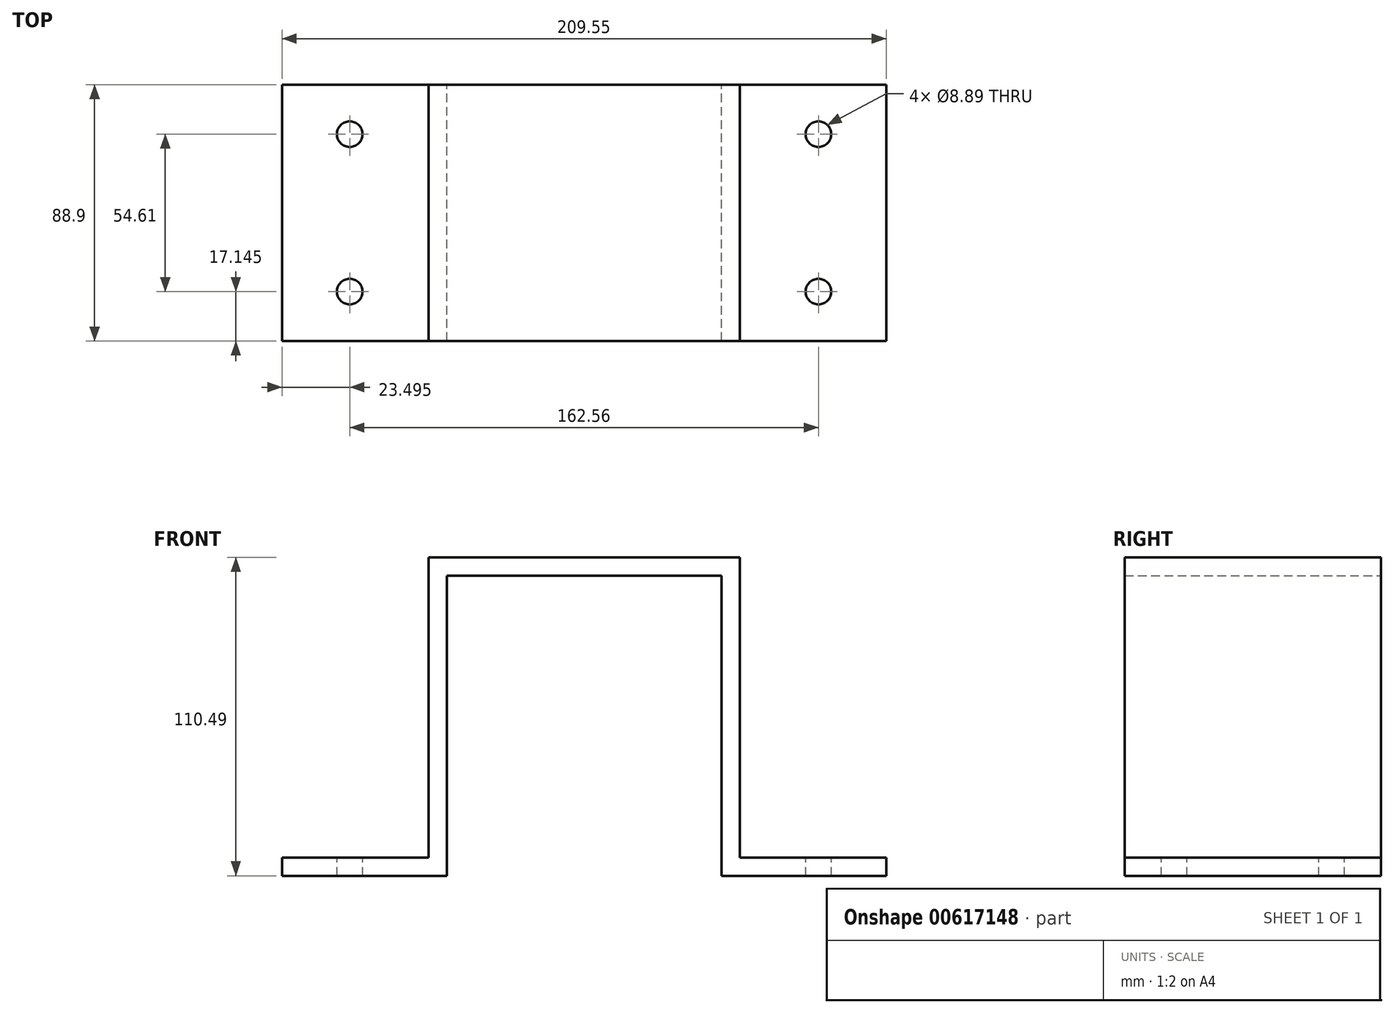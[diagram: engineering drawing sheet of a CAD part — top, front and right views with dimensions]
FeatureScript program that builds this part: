
annotation { "Feature Type Name" : "Feature", "Feature Type Description" : "" }
export const myFeature = defineFeature(function(context is Context, id is Id, definition is map)
    precondition{}
    {
        {
            var Q0;
            Q0=qCreatedBy(makeId("Front.planeOp"),FACE);
            var sketch = newSketch(context, id + "F0", { "sketchPlane" : qUnion([Q0])});
            skLineSegment(sketch, "E0", {"start": v(0, 0) * mm, "end": v(0, 104.14) * mm});
            skLineSegment(sketch, "E1", {"start": v(101.6, 97.8) * mm, "end": v(6.35, 97.8) * mm});
            skLineSegment(sketch, "E2", {"start": v(6.35, 97.8) * mm, "end": v(6.35, 0) * mm});
            skLineSegment(sketch, "E3", {"start": v(6.35, 0) * mm, "end": v(6.35, -6.35) * mm});
            skLineSegment(sketch, "E4", {"start": v(6.35, -6.35) * mm, "end": v(-50.8, -6.35) * mm});
            skLineSegment(sketch, "E5", {"start": v(-50.8, -6.35) * mm, "end": v(-50.8, 0) * mm});
            skLineSegment(sketch, "E6", {"start": v(-50.8, 0) * mm, "end": v(0, 0) * mm});
            skLineSegment(sketch, "E7", {"start": v(101.6, 97.8) * mm, "end": v(101.6, 0) * mm});
            skLineSegment(sketch, "E8", {"start": v(101.6, 0) * mm, "end": v(101.6, -6.35) * mm});
            skLineSegment(sketch, "E9", {"start": v(101.6, -6.35) * mm, "end": v(158.75, -6.35) * mm});
            skLineSegment(sketch, "E10", {"start": v(158.75, -6.35) * mm, "end": v(158.75, 0) * mm});
            skLineSegment(sketch, "E11", {"start": v(158.75, 0) * mm, "end": v(107.95, 0) * mm});
            skLineSegment(sketch, "E12", {"start": v(107.95, 0) * mm, "end": v(107.95, 75.72) * mm});
            skLineSegment(sketch, "E13", {"start": v(0, 104.14) * mm, "end": v(107.95, 104.14) * mm});
            skLineSegment(sketch, "E14", {"start": v(107.95, 104.14) * mm, "end": v(107.95, 75.72) * mm});
            skSolve(sketch);
        }
        {
            var Q0;
            Q0=makeQuery(id+"F0.imprint","IMPRINT",FACE,{"disambiguationData":[TD([[makeQuery(id+"F0.imprint","IMPRINT",EDGE,{"derivedFrom":sQuery(id+"F0.wireOp",EDGE,"E0")}),-1.0]])]});
            extrude(context, id + "F1", {"entities" : qUnion([Q0]), "depth" : 88.9 * mm, "offsetDistance" : 25.4 * mm});
        }
        {
            var Q0;
            Q0=makeQuery(id+"F1.opExtrude","SWEPT_FACE",FACE,{"disambiguationData":[OSD([sQuery(id+"F0.wireOp",EDGE,"E6")])]});
            var sketch = newSketch(context, id + "F2", { "sketchPlane" : qUnion([Q0])});
            skCircle(sketch, "E15", {"center": v(-27.3, -17.14) * mm, "radius": 4.45 * mm});
            skCircle(sketch, "E16", {"center": v(-27.3, -71.76) * mm, "radius": 4.45 * mm});
            skCircle(sketch, "E17", {"center": v(135.26, -17.14) * mm, "radius": 4.45 * mm});
            skCircle(sketch, "E18", {"center": v(135.26, -71.76) * mm, "radius": 4.45 * mm});
            skSolve(sketch);
        }
        {
            var Q0;
            Q0=makeQuery(id+"F2.imprint","IMPRINT",FACE,{"disambiguationData":[TD([[makeQuery(id+"F2.imprint","IMPRINT",EDGE,{"derivedFrom":sQuery(id+"F2.wireOp",EDGE,"E15")}),1.0]])]});
            var Q1;
            Q1=makeQuery(id+"F2.imprint","IMPRINT",FACE,{"disambiguationData":[TD([[makeQuery(id+"F2.imprint","IMPRINT",EDGE,{"derivedFrom":sQuery(id+"F2.wireOp",EDGE,"E16")}),1.0]])]});
            var Q2;
            Q2=makeQuery(id+"F2.imprint","IMPRINT",FACE,{"disambiguationData":[TD([[makeQuery(id+"F2.imprint","IMPRINT",EDGE,{"derivedFrom":sQuery(id+"F2.wireOp",EDGE,"E18")}),1.0]])]});
            var Q3;
            Q3=makeQuery(id+"F2.imprint","IMPRINT",FACE,{"disambiguationData":[TD([[makeQuery(id+"F2.imprint","IMPRINT",EDGE,{"derivedFrom":sQuery(id+"F2.wireOp",EDGE,"E17")}),1.0]])]});
            extrude(context, id + "F3", {"entities" : qUnion([Q0, Q1, Q2, Q3]), "operationType" : NewBodyOperationType.REMOVE, "endBound" : BoundingType.THROUGH_ALL, "oppositeDirection" : true, "depth" : 25.4 * mm, "offsetDistance" : 25.4 * mm});
        }
    });
